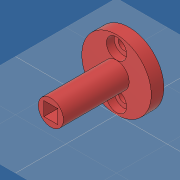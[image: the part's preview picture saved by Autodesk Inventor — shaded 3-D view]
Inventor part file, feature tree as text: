
AUTODESK INVENTOR PART (.ipt)
format: ipt  version: 2019 (Build 230136000, 136)  size: 125,440 bytes
history: native  units: mm
features: extrude x4, sketch x1
ambient origin geometry x8: Origin, YZ Plane, XZ Plane, XY Plane, X Axis, Y Axis, Z Axis, Center Point
bodies: Volumenkörper1 (feature_tree)
feature tree (5):
  sketch  "Skizze1"  dims[d0=27.5mm d1=10.0mm d6=5.0mm d7=0.0mm d25=5.5mm d28=8.0mm d29=18.0mm d30=4.5mm d33=3.0mm d34=0.0mm d35=26.0mm d36=0.0mm d43=4.0mm d44=3.5mm d45=0.0mm]
  extrude  "Extrusion1"  Depth=10.0mm
  extrude  "Extrusion8"  Depth=5.0mm TaperAngle=0.0deg
  extrude  "Extrusion9"  Depth=5.5mm
  extrude  "Extrusion12"  Depth=3.5mm
